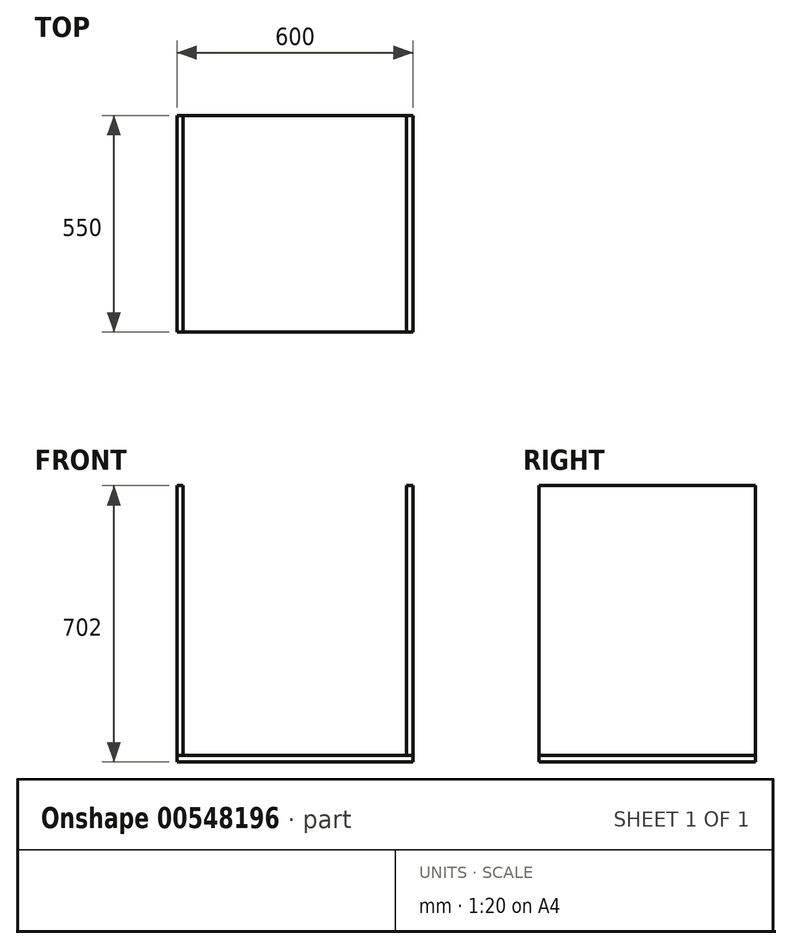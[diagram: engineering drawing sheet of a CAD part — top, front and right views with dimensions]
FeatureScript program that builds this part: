
annotation { "Feature Type Name" : "Feature", "Feature Type Description" : "" }
export const myFeature = defineFeature(function(context is Context, id is Id, definition is map)
    precondition{}
    {
        {
            var Q0;
            Q0=qCreatedBy(makeId("Top.planeOp"),FACE);
            var sketch = newSketch(context, id + "F0", { "sketchPlane" : qUnion([Q0])});
            skLineSegment(sketch, "E0.bottom", {"start": v(0, 0) * mm, "end": v(600, 0) * mm});
            skLineSegment(sketch, "E0.top", {"start": v(0, 550) * mm, "end": v(600, 550) * mm});
            skLineSegment(sketch, "E0.left", {"start": v(0, 0) * mm, "end": v(0, 550) * mm});
            skLineSegment(sketch, "E0.right", {"start": v(600, 0) * mm, "end": v(600, 550) * mm});
            skSolve(sketch);
        }
        {
            var Q0;
            Q0=makeQuery(id+"F0.imprint","IMPRINT",FACE,{"disambiguationData":[TD([[makeQuery(id+"F0.imprint","IMPRINT",EDGE,{"derivedFrom":sQuery(id+"F0.wireOp",EDGE,"E0.bottom")}),1.0]])]});
            extrude(context, id + "F1", {"entities" : qUnion([Q0]), "depth" : 16 * mm, "offsetDistance" : 25 * mm});
        }
        {
            var Q0;
            Q0=makeQuery(id+"F1.opExtrude","CAP_FACE",FACE,{"disambiguationData":[OSD([sQuery(id+"F0.wireOp",EDGE,"E0.bottom"),sQuery(id+"F0.wireOp",EDGE,"E0.top"),sQuery(id+"F0.wireOp",EDGE,"E0.left"),sQuery(id+"F0.wireOp",EDGE,"E0.right")])],"isStart":false});
            var sketch = newSketch(context, id + "F2", { "sketchPlane" : qUnion([Q0])});
            skLineSegment(sketch, "E1.bottom", {"start": v(0, 0) * mm, "end": v(16, 0) * mm});
            skLineSegment(sketch, "E1.top", {"start": v(0, 550) * mm, "end": v(16, 550) * mm});
            skLineSegment(sketch, "E1.left", {"start": v(0, 0) * mm, "end": v(0, 550) * mm});
            skLineSegment(sketch, "E1.right", {"start": v(16, 0) * mm, "end": v(16, 550) * mm});
            skSolve(sketch);
        }
        {
            var Q0;
            Q0=makeQuery(id+"F2.imprint","IMPRINT",FACE,{"disambiguationData":[TD([[makeQuery(id+"F2.imprint","IMPRINT",EDGE,{"derivedFrom":sQuery(id+"F2.wireOp",EDGE,"E1.bottom")}),1.0]])]});
            extrude(context, id + "F3", {"entities" : qUnion([Q0]), "depth" : (850 - 48 - 16 - 100) * mm, "offsetDistance" : 25 * mm});
        }
        {
            var Q0;
            {var subQ0=sQuery(id+"F2.wireOp",EDGE,"E1.right");Q0=makeQuery(id+"F2.imprint","IMPRINT",FACE,{"disambiguationData":[TD([[makeQuery(id+"F2.imprint","IMPRINT",EDGE,{"derivedFrom":subQ0}),-1.0]])]});}
            var sketch = newSketch(context, id + "F4", { "sketchPlane" : qUnion([Q0])});
            skLineSegment(sketch, "E2.bottom", {"start": v(584, 0) * mm, "end": v(600, 0) * mm});
            skLineSegment(sketch, "E2.top", {"start": v(584, 550) * mm, "end": v(600, 550) * mm});
            skLineSegment(sketch, "E2.left", {"start": v(584, 0) * mm, "end": v(584, 550) * mm});
            skLineSegment(sketch, "E2.right", {"start": v(600, 0) * mm, "end": v(600, 550) * mm});
            skSolve(sketch);
        }
        {
            var Q0;
            Q0=makeQuery(id+"F4.imprint","IMPRINT",FACE,{"disambiguationData":[TD([[makeQuery(id+"F4.imprint","IMPRINT",EDGE,{"derivedFrom":sQuery(id+"F4.wireOp",EDGE,"E2.bottom")}),1.0]])]});
            extrude(context, id + "F5", {"entities" : qUnion([Q0]), "depth" : (850 - 16 - 48 - 100) * mm, "offsetDistance" : 25 * mm});
        }
    });
